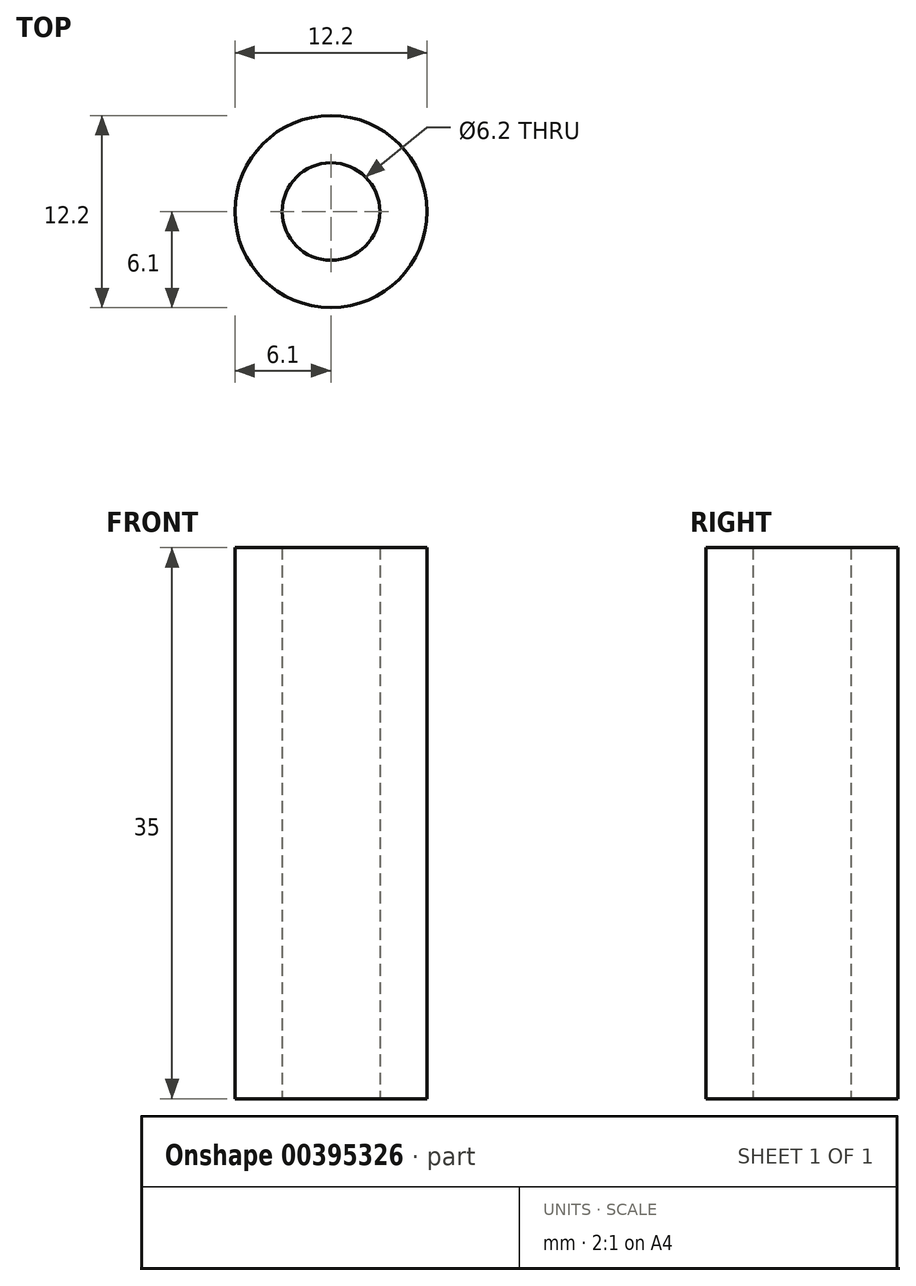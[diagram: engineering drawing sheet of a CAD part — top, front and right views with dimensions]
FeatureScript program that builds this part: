
annotation { "Feature Type Name" : "Feature", "Feature Type Description" : "" }
export const myFeature = defineFeature(function(context is Context, id is Id, definition is map)
    precondition{}
    {
        {
            var Q0;
            Q0=qCreatedBy(makeId("Top.planeOp"),FACE);
            var sketch = newSketch(context, id + "F0", { "sketchPlane" : qUnion([Q0])});
            skCircle(sketch, "E0", {"center": v(0, 0) * mm, "radius": 6.1 * mm});
            skCircle(sketch, "E1", {"center": v(0, 0) * mm, "radius": 3.1 * mm});
            skSolve(sketch);
        }
        {
            var Q0;
            Q0=qSketchRegion(id+"F0",true);
            extrude(context, id + "F1", {"entities" : qUnion([Q0]), "depth" : 35 * mm});
        }
    });
